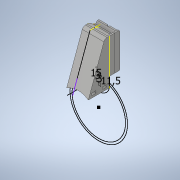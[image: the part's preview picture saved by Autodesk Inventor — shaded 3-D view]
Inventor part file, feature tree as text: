
AUTODESK INVENTOR PART (.ipt)
format: ipt  version: 2021.1 (Build 251245010, 245A)  size: 216,064 bytes
history: mixed  units: in
note: dims shown in document units (in); Inventor stores cm internally (conversion verified against a paired STEP export)
features: extrude x8, sketch x2, plane x1, other x1, fillet x1, imported_body x1
ambient origin geometry x8: Origin, YZ Plane, XZ Plane, XY Plane, X Axis, Y Axis, Z Axis, Center Point
bodies: Solid1 (imported_parasolid), Body1 (imported_parasolid)
feature tree (14):
  plane  "Arbeitsebene2"
  other  "Trennen1"
  sketch  "Skizze2"  dims[d0=0.0in d1=0.3937in d2=0.0in]
  extrude  "Extrusion1"  Depth=0.3937in TaperAngle=0.0deg
  extrude  "Extrusion2"  Depth=0.3937in TaperAngle=0.0deg
  extrude  "Extrusion3"  Depth=0.3937in TaperAngle=0.0deg
  sketch  "Skizze3"  dims[d3=0.5906in d4=0.3937in d5=0.0in d6=0.3937in d7=0.0in d8=0.4528in d10=0.3937in d11=0.0in d12=0.1181in d13=0.1181in d14=1.0236in d15=0.0in d16=0.7874in d17=0.0in d18=0.3937in d19=0.0in d20=0.1575in d21=0.0in d22=0.1969in]
  extrude  "Extrusion4"  Depth=0.1969in
  extrude  "Extrusion5"  Depth=0.3937in TaperAngle=0.0deg
  extrude  "Extrusion6"  Depth=0.1181in
  extrude  "Extrusion7"  Depth=0.1181in
  extrude  "Extrusion8"  Depth=1.0236in TaperAngle=0.0deg
  fillet  "Rundung1"  Radius=0.7874in
  imported_body  NMx_Import_Brep_tag  [imported B-rep: ~42 faces, bbox_mm=[32.0, 66.6, 46.740418]]
